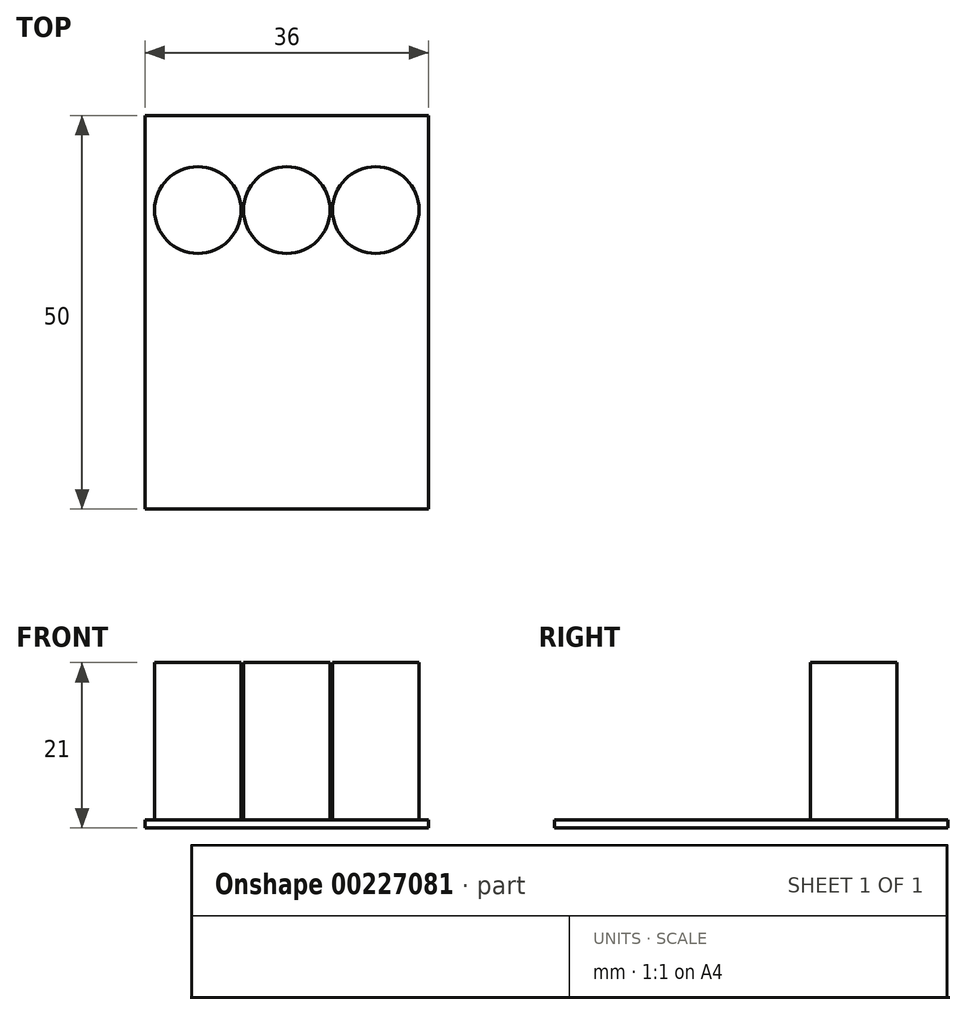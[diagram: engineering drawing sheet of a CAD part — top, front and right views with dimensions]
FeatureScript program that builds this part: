
annotation { "Feature Type Name" : "Feature", "Feature Type Description" : "" }
export const myFeature = defineFeature(function(context is Context, id is Id, definition is map)
    precondition{}
    {
        {
            var Q0;
            Q0=qCreatedBy(makeId("Top.planeOp"),FACE);
            var sketch = newSketch(context, id + "F0", { "sketchPlane" : qUnion([Q0])});
            skLineSegment(sketch, "E0.bottom", {"start": v(18, -25) * mm, "end": v(-18, -25) * mm});
            skLineSegment(sketch, "E0.top", {"start": v(18, 25) * mm, "end": v(-18, 25) * mm});
            skLineSegment(sketch, "E0.left", {"start": v(18, -25) * mm, "end": v(18, 25) * mm});
            skLineSegment(sketch, "E0.right", {"start": v(-18, -25) * mm, "end": v(-18, 25) * mm});
            skPoint(sketch, "E0.middle", {"position": v(0, 0) * mm});
            skSolve(sketch);
        }
        {
            var Q0;
            Q0=makeQuery(id+"F0.imprint","IMPRINT",FACE,{"disambiguationData":[TD([[makeQuery(id+"F0.imprint","IMPRINT",EDGE,{"derivedFrom":sQuery(id+"F0.wireOp",EDGE,"E0.bottom")}),-1.0]])]});
            extrude(context, id + "F1", {"entities" : qUnion([Q0]), "depth" : 1 * mm});
        }
        {
            var Q0;
            Q0=makeQuery(id+"F1.opExtrude","CAP_FACE",FACE,{"disambiguationData":[OSD([sQuery(id+"F0.wireOp",EDGE,"E0.bottom"),sQuery(id+"F0.wireOp",EDGE,"E0.top"),sQuery(id+"F0.wireOp",EDGE,"E0.left"),sQuery(id+"F0.wireOp",EDGE,"E0.right")])],"isStart":false});
            var sketch = newSketch(context, id + "F2", { "sketchPlane" : qUnion([Q0])});
            skCircle(sketch, "E1", {"center": v(-11.3, 13) * mm, "radius": 5.5 * mm});
            skCircle(sketch, "E2", {"center": v(0, 13) * mm, "radius": 5.5 * mm});
            skCircle(sketch, "E3", {"center": v(11.3, 13) * mm, "radius": 5.5 * mm});
            skLineSegment(sketch, "E4", {"start": v(0, 25) * mm, "end": v(0, -25) * mm, "construction": true});
            skSolve(sketch);
        }
        {
            var Q0;
            Q0=makeQuery(id+"F2.imprint","IMPRINT",FACE,{"disambiguationData":[TD([[makeQuery(id+"F2.imprint","IMPRINT",EDGE,{"derivedFrom":sQuery(id+"F2.wireOp",EDGE,"E1")}),1.0]])]});
            var Q1;
            Q1=makeQuery(id+"F2.imprint","IMPRINT",FACE,{"disambiguationData":[TD([[makeQuery(id+"F2.imprint","IMPRINT",EDGE,{"derivedFrom":sQuery(id+"F2.wireOp",EDGE,"E2")}),1.0]])]});
            var Q2;
            Q2=makeQuery(id+"F2.imprint","IMPRINT",FACE,{"disambiguationData":[TD([[makeQuery(id+"F2.imprint","IMPRINT",EDGE,{"derivedFrom":sQuery(id+"F2.wireOp",EDGE,"E3")}),1.0]])]});
            extrude(context, id + "F3", {"entities" : qUnion([Q0, Q1, Q2]), "operationType" : NewBodyOperationType.ADD, "depth" : 20 * mm});
        }
    });
